# Revit family: Sanitary_Mirrors_Svedholm_Slim
name_source: partatom
category: Furniture
revit_build: Autodesk Revit 2018 (Build: 20190510_1515(x64)
units: mm (PartAtom-declared; Revit-internal decimal feet)

## family parameters
Cut with Voids When Loaded = No
Host = Face
OmniClass Number = 23.21.11.00
OmniClass Title = Commercial Furniture
Room Calculation Point = No
Shared = No

## types (2) — shared parameters
BIMobject category = Accessories
Default Elevation = 1219 mm
Description = A mirror with a thin frame of satin brushed stainless steel, with concealed mounting plate that allows the mirror to hang flush.
Design country = Sweden
Edition number = 1
IFC Classification = Object
Main material = Svedholm - Metal - Stainless Steel
Manufacturer = Svedholm
Manufacturer country = Sweden
Manufacturer name = Svedholm
Material main = Powder coated steel
Model = Slim
OmniClass Code = 23-21 11 00
OmniClass Description = Commercial Furniture
Product Guid = 1915c2d7-7e75-43ea-a592-785a7908f1c2
Product SKU = Slits-RWC-handles
Product data url = https://bimobject.com
Product family = Slits
Product group = Accessories
Product name = Slits RWC handles
Product url = https://www.svedholm.se
QR code = https://bimobject.com
URL = https://www.svedholm.se
Underconstruction material = Svedholm - Glass - Mirror
Uniclass 2015 Code = Zz_30_60
Uniclass 2015 Name = Objects

## per-type parameters (varying)
| type | ART - (109.100.001) | ART - (109.100.002) |
| ART - (109.100.001) Dimensions - (1800x300mm) | Yes | No |
| ART - (109.100.002) Dimensions - (600x450mm) | No | Yes |

## geometry (parser evidence)
native form markers: Sweep x4
no freeform markers — native parametric forms only
